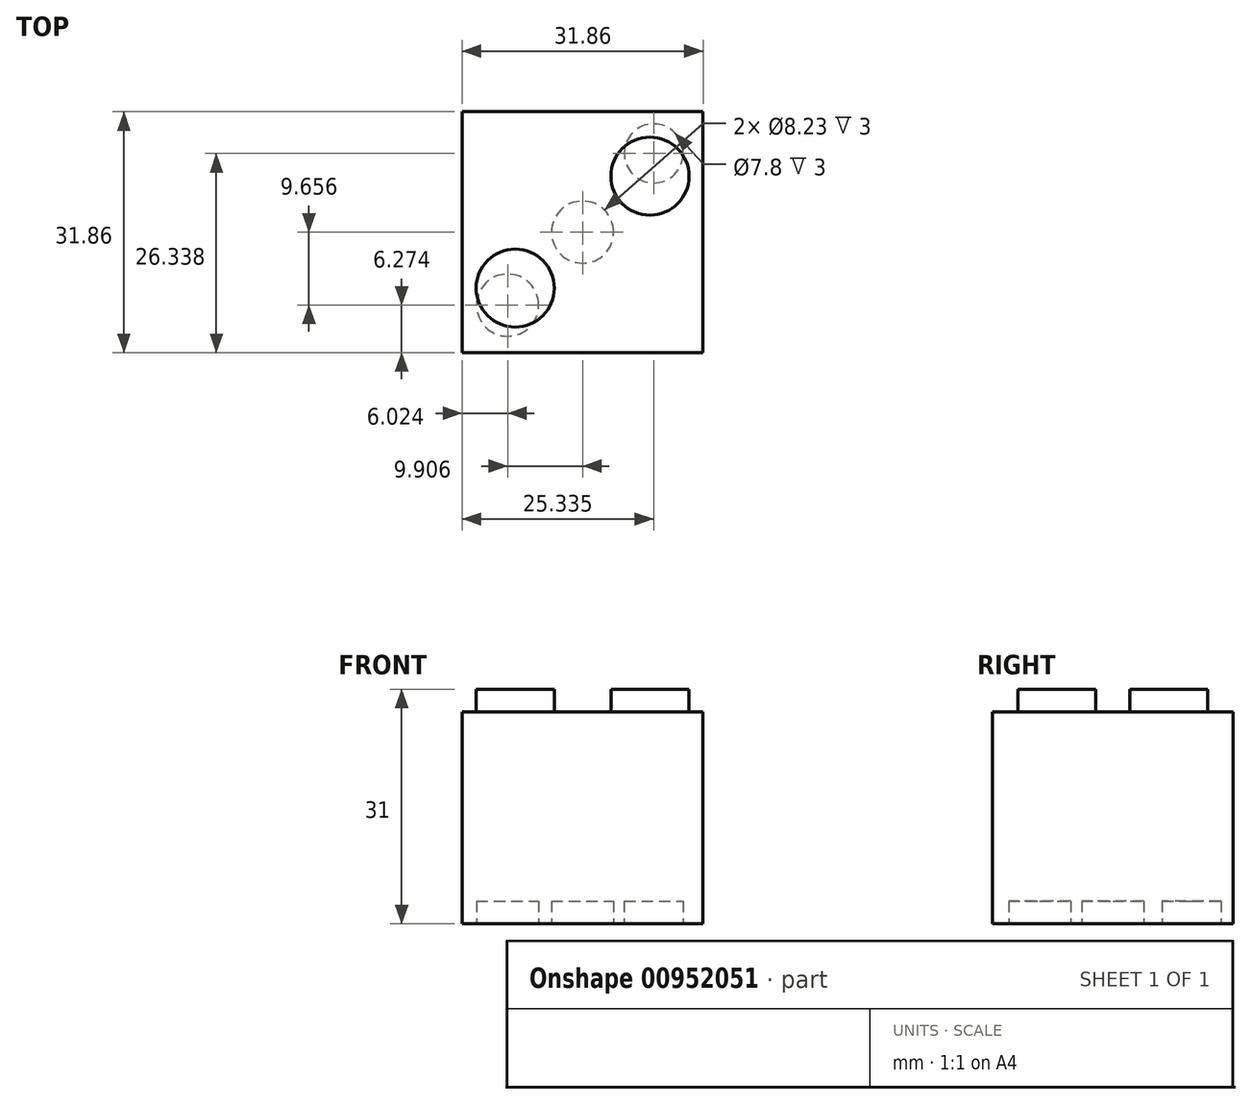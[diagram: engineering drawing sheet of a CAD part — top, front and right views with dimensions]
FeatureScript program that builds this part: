
annotation { "Feature Type Name" : "Feature", "Feature Type Description" : "" }
export const myFeature = defineFeature(function(context is Context, id is Id, definition is map)
    precondition{}
    {
        {
            var Q0;
            Q0=qCreatedBy(makeId("Top.planeOp"),FACE);
            var sketch = newSketch(context, id + "F0", { "sketchPlane" : qUnion([Q0])});
            skLineSegment(sketch, "E0.bottom", {"start": v(-15.93, 15.93) * mm, "end": v(15.93, 15.93) * mm});
            skLineSegment(sketch, "E0.top", {"start": v(-15.93, -15.93) * mm, "end": v(15.93, -15.93) * mm});
            skLineSegment(sketch, "E0.left", {"start": v(-15.93, 15.93) * mm, "end": v(-15.93, -15.93) * mm});
            skLineSegment(sketch, "E0.right", {"start": v(15.93, 15.93) * mm, "end": v(15.93, -15.93) * mm});
            skPoint(sketch, "E0.middle", {"position": v(0, 0) * mm});
            skSolve(sketch);
        }
        {
            var Q0;
            Q0=makeQuery(id+"F0.imprint","IMPRINT",FACE,{"disambiguationData":[TD([[makeQuery(id+"F0.imprint","IMPRINT",EDGE,{"derivedFrom":sQuery(id+"F0.wireOp",EDGE,"E0.bottom")}),-1.0]])]});
            extrude(context, id + "F1", {"entities" : qUnion([Q0]), "depth" : 31 * mm, "offsetDistance" : 25 * mm});
        }
        {
            var Q0;
            Q0=makeQuery(id+"F1.opExtrude","CAP_FACE",FACE,{"disambiguationData":[OSD([sQuery(id+"F0.wireOp",EDGE,"E0.bottom"),sQuery(id+"F0.wireOp",EDGE,"E0.top"),sQuery(id+"F0.wireOp",EDGE,"E0.left"),sQuery(id+"F0.wireOp",EDGE,"E0.right")])],"isStart":false});
            var sketch = newSketch(context, id + "F2", { "sketchPlane" : qUnion([Q0])});
            skCircle(sketch, "E1", {"center": v(-8.9, 7.4) * mm, "radius": 5.16 * mm});
            skCircle(sketch, "E2.MirrorC", {"center": v(8.9, 7.4) * mm, "radius": 5.16 * mm});
            skCircle(sketch, "E3.MirrorC", {"center": v(-8.9, -7.4) * mm, "radius": 5.16 * mm});
            skCircle(sketch, "E4.MirrorC", {"center": v(8.9, -7.4) * mm, "radius": 5.16 * mm});
            skSolve(sketch);
        }
        {
            var Q0;
            Q0=makeQuery(id+"F2.imprint","IMPRINT",FACE,{"disambiguationData":[TD([[makeQuery(id+"F2.imprint","IMPRINT",EDGE,{"derivedFrom":sQuery(id+"F2.wireOp",EDGE,"E1")}),1.0]])]});
            var Q1;
            Q1=makeQuery(id+"F2.imprint","IMPRINT",FACE,{"disambiguationData":[TD([[makeQuery(id+"F2.imprint","IMPRINT",EDGE,{"derivedFrom":sQuery(id+"F2.wireOp",EDGE,"E2.MirrorC")}),-1.0]])]});
            var Q2;
            Q2=makeQuery(id+"F2.imprint","IMPRINT",FACE,{"disambiguationData":[TD([[makeQuery(id+"F2.imprint","IMPRINT",EDGE,{"derivedFrom":sQuery(id+"F2.wireOp",EDGE,"E4.MirrorC")}),1.0]])]});
            var Q3;
            Q3=makeQuery(id+"F2.imprint","IMPRINT",FACE,{"disambiguationData":[TD([[makeQuery(id+"F2.imprint","IMPRINT",EDGE,{"derivedFrom":sQuery(id+"F2.wireOp",EDGE,"E3.MirrorC")}),-1.0]])]});
            extrude(context, id + "F3", {"entities" : qUnion([Q0, Q1, Q2, Q3]), "operationType" : NewBodyOperationType.REMOVE, "oppositeDirection" : true, "depth" : 3 * mm, "offsetDistance" : 25 * mm});
        }
        {
            var Q0;
            Q0=makeQuery(id+"F1.opExtrude","CAP_FACE",FACE,{"disambiguationData":[OSD([sQuery(id+"F0.wireOp",EDGE,"E0.bottom"),sQuery(id+"F0.wireOp",EDGE,"E0.top"),sQuery(id+"F0.wireOp",EDGE,"E0.left"),sQuery(id+"F0.wireOp",EDGE,"E0.right")])],"isStart":true});
            var sketch = newSketch(context, id + "F4", { "sketchPlane" : qUnion([Q0])});
            skCircle(sketch, "E5", {"center": v(-9.9, 9.66) * mm, "radius": 4.11 * mm});
            skCircle(sketch, "E6", {"center": v(0, 0) * mm, "radius": 4.11 * mm});
            skCircle(sketch, "E7", {"center": v(9.4, -10.4) * mm, "radius": 3.9 * mm});
            skSolve(sketch);
        }
        {
            var Q0;
            Q0=makeQuery(id+"F4.imprint","IMPRINT",FACE,{"disambiguationData":[TD([[makeQuery(id+"F4.imprint","IMPRINT",EDGE,{"derivedFrom":sQuery(id+"F4.wireOp",EDGE,"E5")}),1.0]])]});
            var Q1;
            Q1=makeQuery(id+"F4.imprint","IMPRINT",FACE,{"disambiguationData":[TD([[makeQuery(id+"F4.imprint","IMPRINT",EDGE,{"derivedFrom":sQuery(id+"F4.wireOp",EDGE,"E6")}),1.0]])]});
            var Q2;
            Q2=makeQuery(id+"F4.imprint","IMPRINT",FACE,{"disambiguationData":[TD([[makeQuery(id+"F4.imprint","IMPRINT",EDGE,{"derivedFrom":sQuery(id+"F4.wireOp",EDGE,"E7")}),1.0]])]});
            extrude(context, id + "F5", {"entities" : qUnion([Q0, Q1, Q2]), "operationType" : NewBodyOperationType.REMOVE, "oppositeDirection" : true, "depth" : 3 * mm, "offsetDistance" : 25 * mm});
        }
    });
